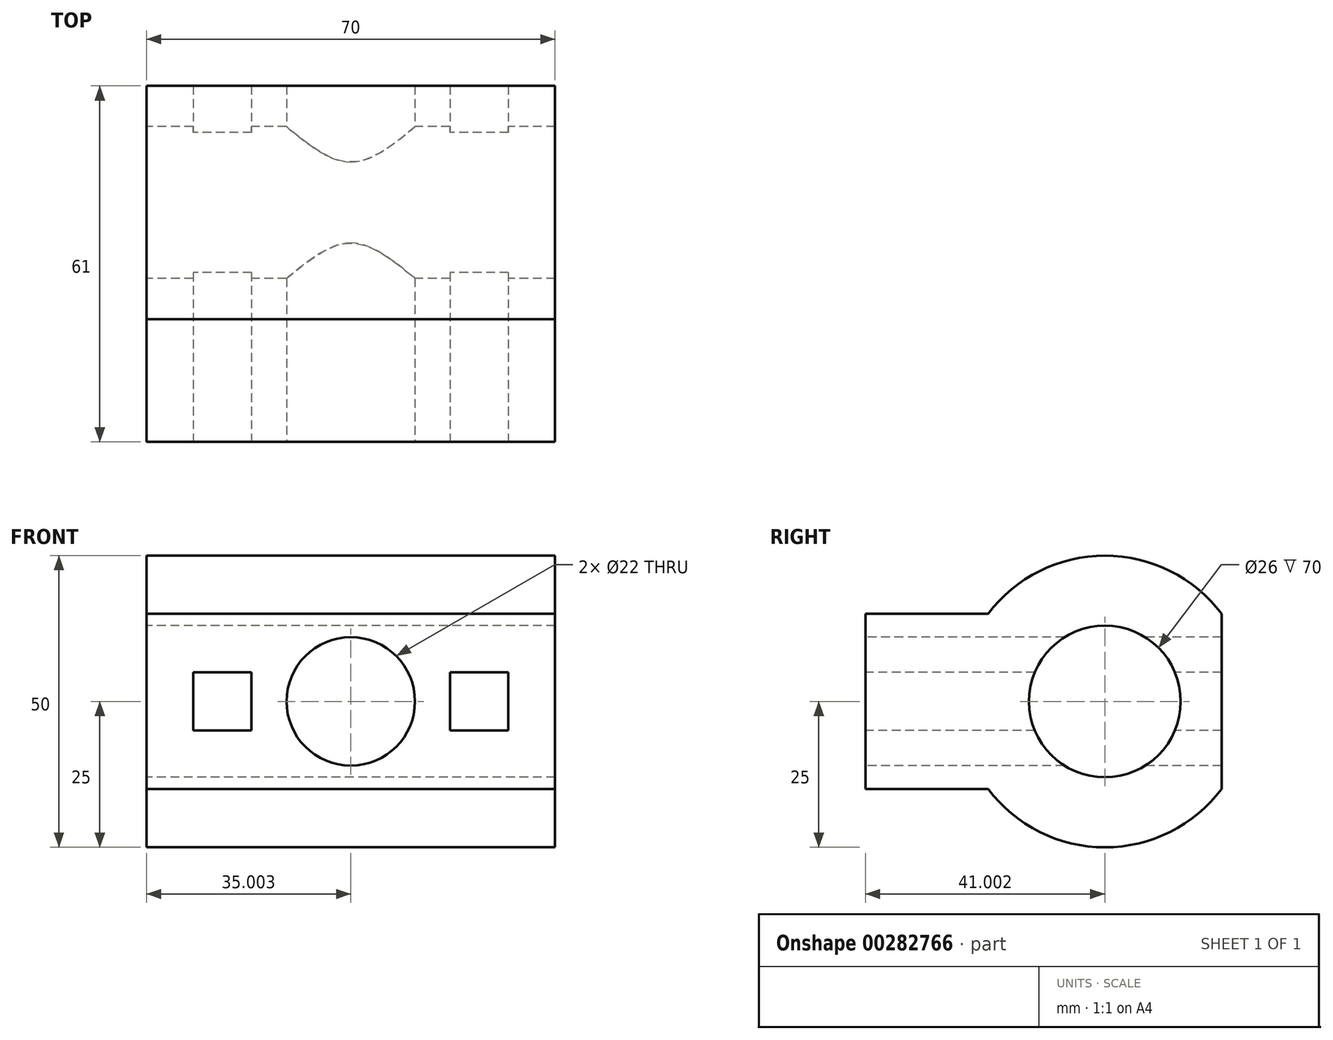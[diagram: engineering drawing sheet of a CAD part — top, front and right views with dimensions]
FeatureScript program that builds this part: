
annotation { "Feature Type Name" : "Feature", "Feature Type Description" : "" }
export const myFeature = defineFeature(function(context is Context, id is Id, definition is map)
    precondition{}
    {
        {
            var Q0;
            Q0=qCreatedBy(makeId("Top.planeOp"),FACE);
            var sketch = newSketch(context, id + "F0", { "sketchPlane" : qUnion([Q0])});
            skLineSegment(sketch, "E0.bottom", {"start": v(-70.74, 106.13) * mm, "end": v(-0.74, 106.13) * mm});
            skLineSegment(sketch, "E0.top", {"start": v(-70.74, 40.13) * mm, "end": v(-0.74, 40.13) * mm});
            skLineSegment(sketch, "E0.left", {"start": v(-70.74, 106.13) * mm, "end": v(-70.74, 40.13) * mm});
            skLineSegment(sketch, "E0.right", {"start": v(-0.74, 106.13) * mm, "end": v(-0.74, 40.13) * mm});
            skSolve(sketch);
        }
        {
            var Q0;
            Q0 = qSketchRegion(id + "F0", true);
            extrude(context, id + "F1", {"entities" : qUnion([Q0]), "depth" : 30 * mm});
        }
        {
            var Q0;
            Q0=makeQuery(id+"F1.opExtrude","SWEPT_FACE",FACE,{"disambiguationData":[OSD([sQuery(id+"F0.wireOp",EDGE,"E0.left")])]});
            var sketch = newSketch(context, id + "F2", { "sketchPlane" : qUnion([Q0])});
            skCircle(sketch, "E1", {"center": v(-81.13, 15) * mm, "radius": 25 * mm});
            skPoint(sketch, "E2.start.orphan", {"position": v(-106.13, 15) * mm});
            skSolve(sketch);
        }
        {
            var Q0;
            {var subQ0=sQuery(id+"F2.wireOp",EDGE,"E1");var subQ1=makeQuery(id+"F1.opExtrude","CAP_EDGE",EDGE,{"disambiguationData":[OSD([sQuery(id+"F0.wireOp",EDGE,"E0.left")])],"isStart":false});var subQ2=makeQuery(id+"F2.imprint","INTERSECT",VERTEX,{"disambiguationData":[OD(0.0)],"derivedFrom":[subQ1,subQ0]});Q0=makeQuery(id+"F2.imprint","IMPRINT",FACE,{"disambiguationData":[TD([[makeQuery(id+"F2.imprint","IMPRINT",EDGE,{"disambiguationData":[TD([[subQ2,1.0]])],"derivedFrom":subQ0}),1.0]])]});}
            var Q1;
            {var subQ0=sQuery(id+"F2.wireOp",EDGE,"E1");var subQ1=makeQuery(id+"F1.opExtrude","CAP_EDGE",EDGE,{"disambiguationData":[OSD([sQuery(id+"F0.wireOp",EDGE,"E0.left")])],"isStart":true});var subQ2=makeQuery(id+"F2.imprint","INTERSECT",VERTEX,{"disambiguationData":[OD(0.0)],"derivedFrom":[subQ1,subQ0]});Q1=makeQuery(id+"F2.imprint","IMPRINT",FACE,{"disambiguationData":[TD([[makeQuery(id+"F2.imprint","IMPRINT",EDGE,{"disambiguationData":[TD([[subQ2,-1.0]])],"derivedFrom":subQ0}),1.0]])]});}
            extrude(context, id + "F3", {"entities" : qUnion([Q0, Q1]), "operationType" : NewBodyOperationType.ADD, "oppositeDirection" : true, "depth" : 70 * mm});
        }
        {
            var Q0;
            {var subQ1=sQuery(id+"F0.wireOp",EDGE,"E0.left");var subQ6=sQuery(id+"F0.wireOp",EDGE,"E0.right");var subQ12=sQuery(id+"F0.wireOp",EDGE,"E0.bottom");Q0=makeQuery(id+"F3.boolean.opBoolean","SPLIT",FACE,{"disambiguationData":[TD([makeQuery(id+"F1.opExtrude","SWEPT_FACE",FACE,{"disambiguationData":[OSD([subQ12])]})])],"derivedFrom":makeQuery(id+"F1.opExtrude","CAP_FACE",FACE,{"disambiguationData":[OSD([subQ12,sQuery(id+"F0.wireOp",EDGE,"E0.top"),subQ1,subQ6])],"isStart":false})});}
            extrude(context, id + "F4", {"entities" : qUnion([Q0]), "operationType" : NewBodyOperationType.REMOVE, "oppositeDirection" : true, "depth" : 30 * mm});
        }
        {
            var Q0;
            {var subQ0=sQuery(id+"F2.wireOp",EDGE,"E1");var subQ1=sQuery(id+"F0.wireOp",EDGE,"E0.left");var subQ2=makeQuery(id+"F1.opExtrude","CAP_EDGE",EDGE,{"disambiguationData":[OSD([subQ1])],"isStart":true});var subQ3=makeQuery(id+"F2.imprint","INTERSECT",VERTEX,{"disambiguationData":[OD(0.0)],"derivedFrom":[subQ2,subQ0]});var subQ5=makeQuery(id+"F1.opExtrude","CAP_EDGE",EDGE,{"disambiguationData":[OSD([subQ1])],"isStart":false});var subQ6=makeQuery(id+"F2.imprint","INTERSECT",VERTEX,{"disambiguationData":[OD(0.0)],"derivedFrom":[subQ5,subQ0]});Q0=makeQuery(id+"F3.boolean.opBoolean","MERGE",FACE,{"derivedFrom":[makeQuery(id+"F1.opExtrude","SWEPT_FACE",FACE,{"disambiguationData":[OSD([subQ1])]}),makeQuery(id+"F3.opExtrude","CAP_FACE",FACE,{"disambiguationData":[OSD([subQ1,subQ0]),TDD([makeQuery(id+"F2.imprint","IMPRINT",EDGE,{"disambiguationData":[TD([[subQ6,1.0]])],"derivedFrom":subQ0}),makeQuery(id+"F2.imprint","IMPRINT",EDGE,{"disambiguationData":[TD([[subQ6,-1.0]])],"derivedFrom":subQ5})])],"isStart":true}),makeQuery(id+"F3.opExtrude","CAP_FACE",FACE,{"disambiguationData":[OSD([subQ1,subQ0]),TDD([makeQuery(id+"F2.imprint","IMPRINT",EDGE,{"disambiguationData":[TD([[subQ3,-1.0]])],"derivedFrom":subQ0}),makeQuery(id+"F2.imprint","IMPRINT",EDGE,{"disambiguationData":[TD([[subQ3,-1.0]])],"derivedFrom":subQ2})])],"isStart":true})]});}
            var sketch = newSketch(context, id + "F5", { "sketchPlane" : qUnion([Q0])});
            skCircle(sketch, "E3", {"center": v(-81.13, 15) * mm, "radius": 13 * mm});
            skSolve(sketch);
        }
        {
            var Q0;
            Q0=sQuery(id+"F5.wireOp",VERTEX,"E3.center");
            var Q1;
            Q1=makeQuery(id+"F1.opExtrude","SWEPT_BODY",BODY,{"disambiguationData":[OSD([sQuery(id+"F0.wireOp",EDGE,"E0.bottom"),sQuery(id+"F0.wireOp",EDGE,"E0.top"),sQuery(id+"F0.wireOp",EDGE,"E0.left"),sQuery(id+"F0.wireOp",EDGE,"E0.right")])]});
            hole(context, id + "F6", {"style" : HoleStyle.SIMPLE, "endStyle" : HoleEndStyle.THROUGH, "holeDiameter" : 26 * mm, "tappedDepth" : 12 * mm, "tapClearance" : 3, "locations" : qUnion([Q0]), "scope" : qUnion([Q1])});
        }
        {
            var Q0;
            Q0=makeQuery(id+"F1.opExtrude","SWEPT_FACE",FACE,{"disambiguationData":[OSD([sQuery(id+"F0.wireOp",EDGE,"E0.top")])]});
            var sketch = newSketch(context, id + "F7", { "sketchPlane" : qUnion([Q0])});
            skCircle(sketch, "E4", {"center": v(-35.74, 15) * mm, "radius": 11 * mm});
            skPoint(sketch, "E4.centerSnap0", {"position": v(-35.74, 30) * mm});
            skPoint(sketch, "E4.centerSnap1", {"position": v(-70.74, 15) * mm});
            skLineSegment(sketch, "E5.bottom", {"start": v(-52.74, 10) * mm, "end": v(-62.74, 10) * mm});
            skLineSegment(sketch, "E5.top", {"start": v(-52.74, 20) * mm, "end": v(-62.74, 20) * mm});
            skLineSegment(sketch, "E5.left", {"start": v(-52.74, 10) * mm, "end": v(-52.74, 20) * mm});
            skLineSegment(sketch, "E5.right", {"start": v(-62.74, 10) * mm, "end": v(-62.74, 20) * mm});
            skPoint(sketch, "E5.middle", {"position": v(-57.74, 15) * mm});
            skLineSegment(sketch, "E6.bottom", {"start": v(-8.74, 10) * mm, "end": v(-18.74, 10) * mm});
            skLineSegment(sketch, "E6.top", {"start": v(-8.74, 20) * mm, "end": v(-18.74, 20) * mm});
            skLineSegment(sketch, "E6.left", {"start": v(-8.74, 10) * mm, "end": v(-8.74, 20) * mm});
            skLineSegment(sketch, "E6.right", {"start": v(-18.74, 10) * mm, "end": v(-18.74, 20) * mm});
            skPoint(sketch, "E6.middle", {"position": v(-13.74, 15) * mm});
            skPoint(sketch, "E7.start.orphan", {"position": v(-0.74, 15) * mm});
            skSolve(sketch);
        }
        {
            var Q0;
            Q0=makeQuery(id+"F7.imprint","IMPRINT",FACE,{"disambiguationData":[TD([[makeQuery(id+"F7.imprint","IMPRINT",EDGE,{"derivedFrom":sQuery(id+"F7.wireOp",EDGE,"E5.bottom")}),-1.0]])]});
            var Q1;
            Q1=makeQuery(id+"F7.imprint","IMPRINT",FACE,{"disambiguationData":[TD([[makeQuery(id+"F7.imprint","IMPRINT",EDGE,{"derivedFrom":sQuery(id+"F7.wireOp",EDGE,"E6.bottom")}),-1.0]])]});
            var Q2;
            Q2=makeQuery(id+"F7.imprint","IMPRINT",FACE,{"disambiguationData":[TD([[makeQuery(id+"F7.imprint","IMPRINT",EDGE,{"derivedFrom":sQuery(id+"F7.wireOp",EDGE,"E4")}),1.0]])]});
            extrude(context, id + "F8", {"entities" : qUnion([Q0, Q1, Q2]), "operationType" : NewBodyOperationType.REMOVE, "oppositeDirection" : true, "depth" : 70 * mm});
        }
    });
